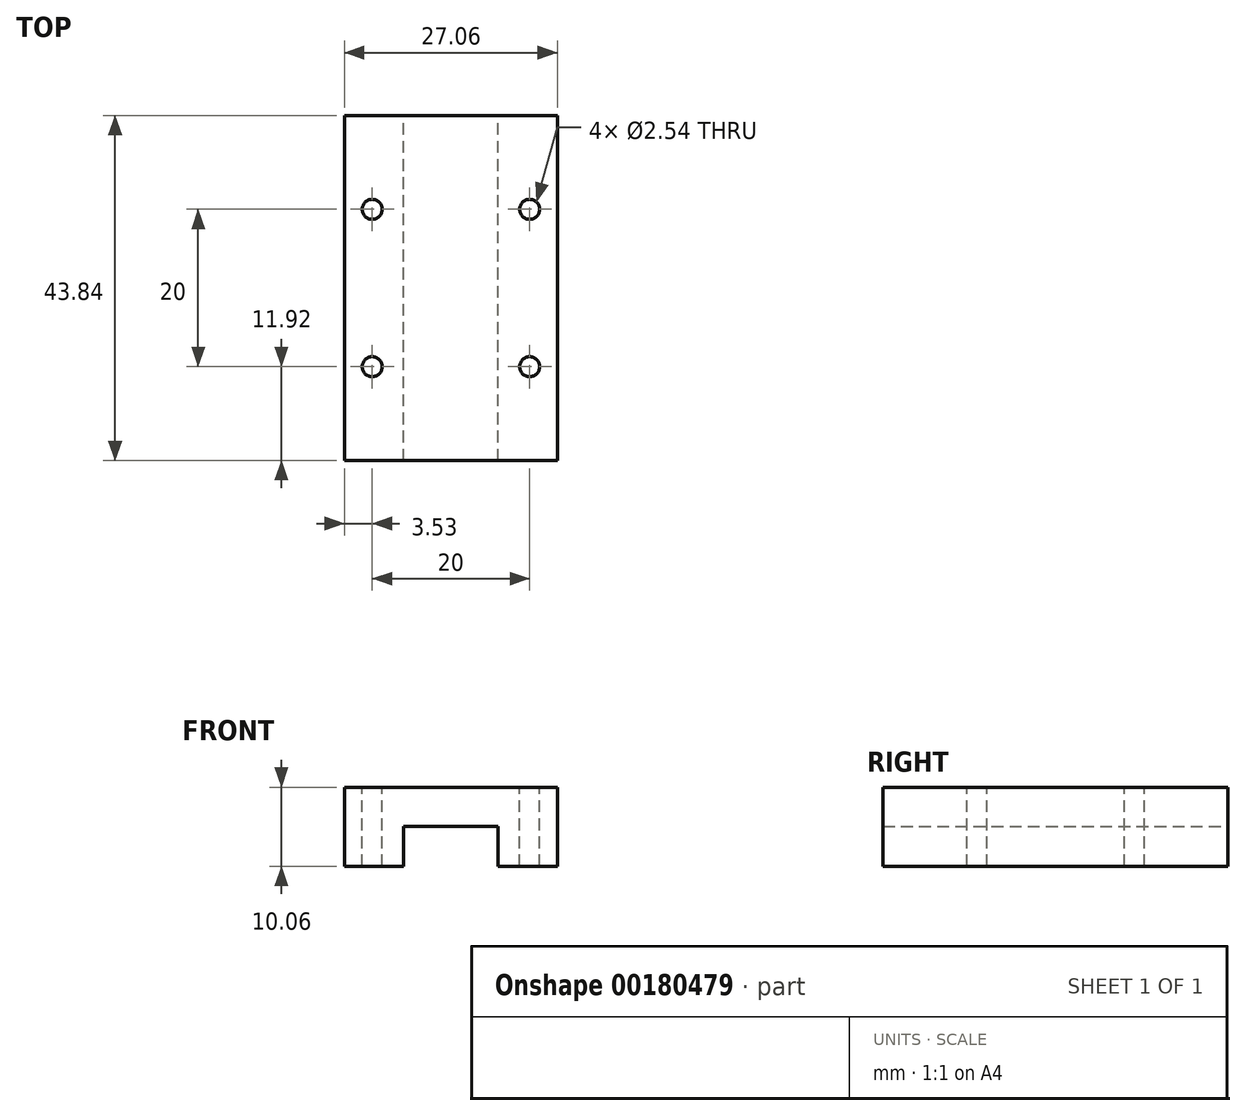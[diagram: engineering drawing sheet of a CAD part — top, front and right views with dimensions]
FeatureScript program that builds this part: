
annotation { "Feature Type Name" : "Feature", "Feature Type Description" : "" }
export const myFeature = defineFeature(function(context is Context, id is Id, definition is map)
    precondition{}
    {
        {
            var Q0;
            Q0=qCreatedBy(makeId("Front.planeOp"),FACE);
            var sketch = newSketch(context, id + "F0", { "sketchPlane" : qUnion([Q0])});
            skLineSegment(sketch, "E0", {"start": v(6.02, 0) * mm, "end": v(6.02, 5.08) * mm});
            skLineSegment(sketch, "E1", {"start": v(6.02, 0) * mm, "end": v(13.53, 0) * mm});
            skLineSegment(sketch, "E2", {"start": v(13.53, 0) * mm, "end": v(13.53, 10.06) * mm});
            skLineSegment(sketch, "E3", {"start": v(13.53, 10.06) * mm, "end": v(0, 10.06) * mm});
            skLineSegment(sketch, "E4", {"start": v(6.02, 5.08) * mm, "end": v(0, 5.08) * mm});
            skLineSegment(sketch, "E5.MirrorCS", {"start": v(-6.02, 5.08) * mm, "end": v(0, 5.08) * mm});
            skLineSegment(sketch, "E6.MirrorCS", {"start": v(-13.53, 10.06) * mm, "end": v(0, 10.06) * mm});
            skLineSegment(sketch, "E7.MirrorCS", {"start": v(-6.02, 0) * mm, "end": v(-13.53, 0) * mm});
            skLineSegment(sketch, "E8.MirrorCS", {"start": v(-6.02, 0) * mm, "end": v(-6.02, 5.08) * mm});
            skLineSegment(sketch, "E9.MirrorCS", {"start": v(-13.53, 0) * mm, "end": v(-13.53, 10.06) * mm});
            skSolve(sketch);
        }
        {
            var Q0;
            Q0 = qSketchRegion(id + "F0", true);
            extrude(context, id + "F1", {"entities" : qUnion([Q0]), "depth" : 43.84 * mm});
        }
        {
            var Q0;
            Q0=makeQuery(id+"F1.opExtrude","SWEPT_FACE",FACE,{"disambiguationData":[OSD([sQuery(id+"F0.wireOp",EDGE,"E3"),sQuery(id+"F0.wireOp",EDGE,"E6.MirrorCS")])]});
            var sketch = newSketch(context, id + "F2", { "sketchPlane" : qUnion([Q0])});
            skCircle(sketch, "E10", {"center": v(10, -11.92) * mm, "radius": 1.27 * mm});
            skLineSegment(sketch, "E11", {"start": v(-13.53, -21.92) * mm, "end": v(13.53, -21.92) * mm, "construction": true});
            skCircle(sketch, "E12.MirrorC", {"center": v(10, -31.92) * mm, "radius": 1.27 * mm});
            skCircle(sketch, "E13.MirrorC", {"center": v(-10, -31.92) * mm, "radius": 1.27 * mm});
            skCircle(sketch, "E14.MirrorC", {"center": v(-10, -11.92) * mm, "radius": 1.27 * mm});
            skSolve(sketch);
        }
        {
            var Q0;
            Q0 = qSketchRegion(id + "F2", true);
            extrude(context, id + "F3", {"entities" : qUnion([Q0]), "operationType" : NewBodyOperationType.REMOVE, "endBound" : BoundingType.UP_TO_NEXT, "oppositeDirection" : true, "depth" : 25.4 * mm});
        }
    });
